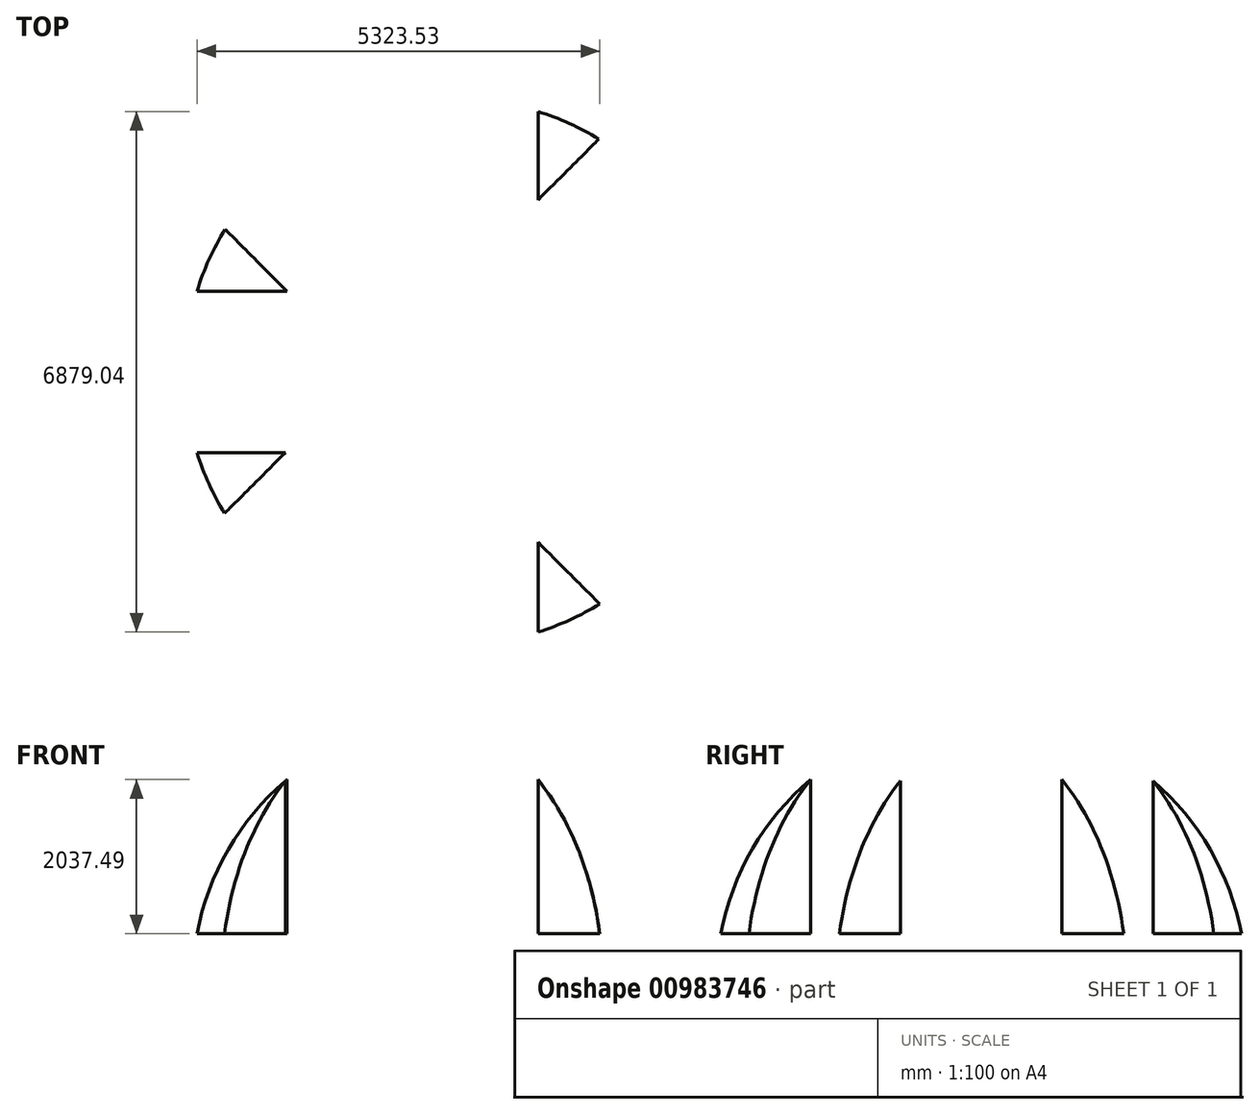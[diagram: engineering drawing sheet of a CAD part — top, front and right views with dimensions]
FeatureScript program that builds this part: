
annotation { "Feature Type Name" : "Feature", "Feature Type Description" : "" }
export const myFeature = defineFeature(function(context is Context, id is Id, definition is map)
    precondition{}
    {
        {
            var Q0;
            Q0=qCreatedBy(makeId("Front.planeOp"),FACE);
            var sketch = newSketch(context, id + "F0", { "sketchPlane" : qUnion([Q0])});
            skLineSegment(sketch, "E0", {"start": v(0, 0) * mm, "end": v(0, 3017.52) * mm});
            skLineSegment(sketch, "E1", {"start": v(0, 0) * mm, "end": v(3601.16, 0) * mm});
            skLineSegment(sketch, "E2", {"start": v(0, 0) * mm, "end": v(-3601.16, 0) * mm});
            skArc(sketch, "E3", {"start": v(3601.16, 0) * mm, "mid": v(0, 3017.52) * mm, "end": v(-3601.16, 0) * mm});
            skSolve(sketch);
        }
        {
            var Q0;
            {var subQ0=sQuery(id+"F0.wireOp",EDGE,"E0");Q0=makeQuery(id+"F0.imprint","IMPRINT",FACE,{"disambiguationData":[TD([[makeQuery(id+"F0.imprint","IMPRINT",EDGE,{"derivedFrom":subQ0}),1.0]])]});}
            var Q1;
            Q1=sQuery(id+"F0.wireOp",EDGE,"E0");
            revolve(context, id + "F1", {"surfaceOperationType" : NewSurfaceOperationType.NEW, "entities" : qUnion([Q0]), "axis" : qUnion([Q1]), "revolveType" : RevolveType.FULL});
        }
        {
            var Q0;
            Q0=qCreatedBy(makeId("Top.planeOp"),FACE);
            cPlane(context, id + "F2", {"entities" : qUnion([Q0]), "cplaneType" : CPlaneType.OFFSET, "offset" : 3048 * mm, "width" : 152.4 * mm, "height" : 152.4 * mm});
        }
        {
            var Q0;
            Q0=qCreatedBy(id+"F2.planeOp",FACE);
            var sketch = newSketch(context, id + "F3", { "sketchPlane" : qUnion([Q0])});
            skLineSegment(sketch, "E4.bottom", {"start": v(5574.51, -1066.8) * mm, "end": v(1066.8, -1066.8) * mm});
            skLineSegment(sketch, "E4.top", {"start": v(5574.51, 1066.8) * mm, "end": v(1066.8, 1066.8) * mm});
            skLineSegment(sketch, "E4.left", {"start": v(5574.51, -1066.8) * mm, "end": v(5574.51, 1066.8) * mm});
            skLineSegment(sketch, "E4.right", {"start": v(-5574.51, -1066.8) * mm, "end": v(-5574.51, 1066.8) * mm});
            skPoint(sketch, "E4.middle", {"position": v(0, 0) * mm});
            skLineSegment(sketch, "E5.bottom", {"start": v(1066.8, 4918.2) * mm, "end": v(-1066.8, 4918.2) * mm});
            skLineSegment(sketch, "E5.top", {"start": v(1066.8, -4918.2) * mm, "end": v(-1066.8, -4918.2) * mm});
            skLineSegment(sketch, "E5.left", {"start": v(1066.8, 4918.2) * mm, "end": v(1066.8, 1066.8) * mm});
            skLineSegment(sketch, "E5.right", {"start": v(-1066.8, 4918.2) * mm, "end": v(-1066.8, 1066.8) * mm});
            skLineSegment(sketch, "E6.trimOffspring", {"start": v(-1066.8, 1066.8) * mm, "end": v(-5574.51, 1066.8) * mm});
            skLineSegment(sketch, "E7.trimOffspring", {"start": v(1066.8, -1066.8) * mm, "end": v(1066.8, -4918.2) * mm});
            skLineSegment(sketch, "E8.trimOffspring", {"start": v(-1066.8, -1066.8) * mm, "end": v(-5574.51, -1066.8) * mm});
            skLineSegment(sketch, "E9.trimOffspring", {"start": v(-1066.8, -1066.8) * mm, "end": v(-1066.8, -4918.2) * mm});
            skSolve(sketch);
        }
        {
            var Q0;
            Q0=makeQuery(id+"F3.imprint","IMPRINT",FACE,{"disambiguationData":[TD([[makeQuery(id+"F3.imprint","IMPRINT",EDGE,{"derivedFrom":sQuery(id+"F3.wireOp",EDGE,"E4.bottom")}),-1.0]])]});
            extrude(context, id + "F4", {"entities" : qUnion([Q0]), "operationType" : NewBodyOperationType.REMOVE, "endBound" : BoundingType.THROUGH_ALL, "oppositeDirection" : true, "depth" : 25.4 * mm, "offsetDistance" : 25.4 * mm});
        }
        {
            var Q0;
            Q0=qCreatedBy(id+"F2.planeOp",FACE);
            var sketch = newSketch(context, id + "F6", { "sketchPlane" : qUnion([Q0])});
            skLineSegment(sketch, "E10.bottom", {"start": v(5050.58, -2643.48) * mm, "end": v(3254.53, -4439.53) * mm});
            skLineSegment(sketch, "E10.top", {"start": v(-2103.2, 4510.3) * mm, "end": v(-3899.24, 2714.24) * mm});
            skLineSegment(sketch, "E10.left", {"start": v(5050.58, -2643.48) * mm, "end": v(2397.23, 9.87) * mm});
            skLineSegment(sketch, "E10.right", {"start": v(3254.53, -4439.53) * mm, "end": v(601.18, -1786.18) * mm});
            skPoint(sketch, "E10.middle", {"position": v(575.67, 35.38) * mm});
            skLineSegment(sketch, "E11", {"start": v(128.82, 35.38) * mm, "end": v(575.67, 35.38) * mm});
            skLineSegment(sketch, "E12", {"start": v(-4624.67, -3419.93) * mm, "end": v(-1194.87, 9.87) * mm});
            skLineSegment(sketch, "E13", {"start": v(3788.92, 4993.66) * mm, "end": v(5584.97, 3197.6) * mm});
            skLineSegment(sketch, "E14", {"start": v(5584.97, 3197.6) * mm, "end": v(2397.23, 9.87) * mm});
            skLineSegment(sketch, "E15", {"start": v(-2768.82, -5156.2) * mm, "end": v(-4624.67, -3419.93) * mm});
            skLineSegment(sketch, "E16.trimOffspring", {"start": v(601.18, 1805.92) * mm, "end": v(3788.92, 4993.66) * mm});
            skLineSegment(sketch, "E17.trimOffspring", {"start": v(601.18, 1805.92) * mm, "end": v(-2103.2, 4510.3) * mm});
            skLineSegment(sketch, "E18.trimOffspring", {"start": v(601.18, -1786.18) * mm, "end": v(-2768.82, -5156.2) * mm});
            skLineSegment(sketch, "E19.trimOffspring", {"start": v(-1194.87, 9.87) * mm, "end": v(-3899.24, 2714.24) * mm});
            skSolve(sketch);
        }
        {
            var Q0;
            Q0 = qSketchRegion(id + "F6", true);
            extrude(context, id + "F7", {"entities" : qUnion([Q0]), "operationType" : NewBodyOperationType.REMOVE, "endBound" : BoundingType.THROUGH_ALL, "oppositeDirection" : true, "depth" : 25.4 * mm, "offsetDistance" : 25.4 * mm});
        }
    });
